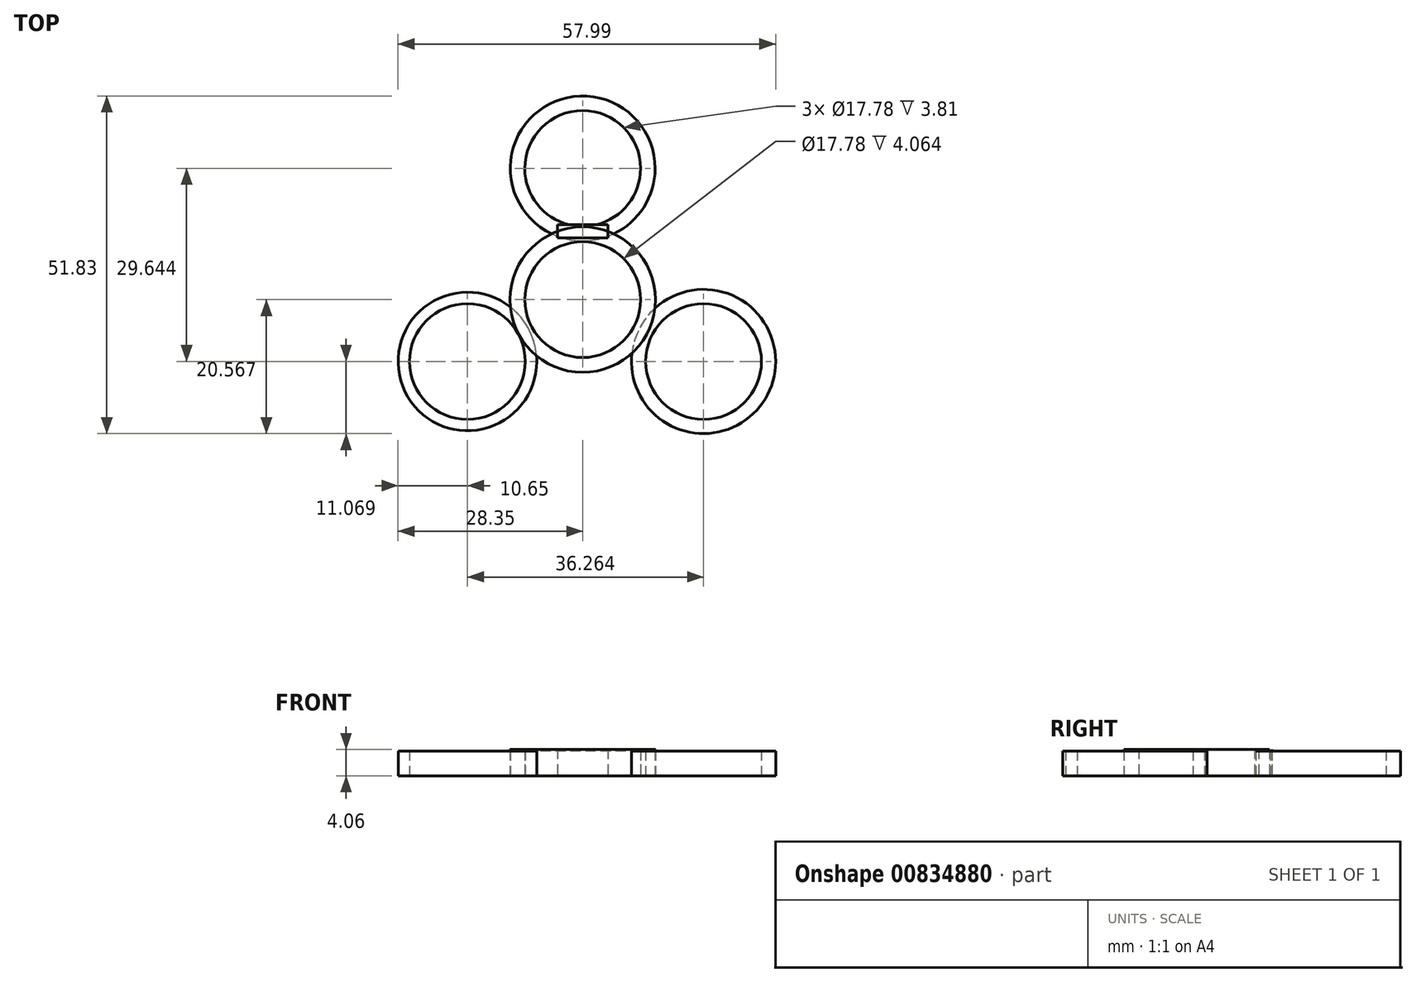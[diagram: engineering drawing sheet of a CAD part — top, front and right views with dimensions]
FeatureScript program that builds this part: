
annotation { "Feature Type Name" : "Feature", "Feature Type Description" : "" }
export const myFeature = defineFeature(function(context is Context, id is Id, definition is map)
    precondition{}
    {
        {
            var Q0;
            Q0=qCreatedBy(makeId("Top.planeOp"),FACE);
            var sketch = newSketch(context, id + "F0", { "sketchPlane" : qUnion([Q0])});
            skCircle(sketch, "E0", {"center": v(0, 25.18) * mm, "radius": 11.12 * mm});
            skCircle(sketch, "E1", {"center": v(-17.7, -4.46) * mm, "radius": 10.65 * mm});
            skCircle(sketch, "E2", {"center": v(18.56, -4.46) * mm, "radius": 11.07 * mm});
            skSolve(sketch);
        }
        {
            var Q0;
            Q0 = qSketchRegion(id + "F0", true);
            extrude(context, id + "F1", {"entities" : qUnion([Q0]), "depth" : 3.8 * mm, "offsetDistance" : 25.4 * mm});
        }
        {
            var Q0;
            Q0=sQuery(id+"F0.wireOp",VERTEX,"E0.center");
            var Q1;
            Q1=sQuery(id+"F0.wireOp",VERTEX,"E1.center");
            var Q2;
            Q2=sQuery(id+"F0.wireOp",VERTEX,"E2.center");
            var Q3;
            Q3=makeQuery(id+"F1.opExtrude","SWEPT_BODY",BODY,{"disambiguationData":[OSD([sQuery(id+"F0.wireOp",EDGE,"E0")])]});
            var Q4;
            Q4=makeQuery(id+"F1.opExtrude","SWEPT_BODY",BODY,{"disambiguationData":[OSD([sQuery(id+"F0.wireOp",EDGE,"E1")])]});
            var Q5;
            Q5=makeQuery(id+"F1.opExtrude","SWEPT_BODY",BODY,{"disambiguationData":[OSD([sQuery(id+"F0.wireOp",EDGE,"E2")])]});
            hole(context, id + "F2", {"style" : HoleStyle.SIMPLE, "endStyle" : HoleEndStyle.THROUGH, "oppositeDirection" : true, "holeDiameter" : 17.78 * mm, "majorDiameter" : 6.35 * mm, "isTappedThrough" : true, "tappedDepth" : 12.7 * mm, "tapClearance" : 3, "locations" : qUnion([Q0, Q1, Q2]), "scope" : qUnion([Q3, Q4, Q5])});
        }
        {
            var Q0;
            Q0=qCreatedBy(makeId("Top.planeOp"),FACE);
            var sketch = newSketch(context, id + "F3", { "sketchPlane" : qUnion([Q0])});
            skCircle(sketch, "E3", {"center": v(0, 5.04) * mm, "radius": 11.17 * mm});
            skSolve(sketch);
        }
        {
            var Q0;
            Q0 = qSketchRegion(id + "F3", true);
            extrude(context, id + "F4", {"entities" : qUnion([Q0]), "depth" : 4.06 * mm, "offsetDistance" : 25.4 * mm});
        }
        {
            var Q0;
            Q0=sQuery(id+"F3.wireOp",VERTEX,"E3.center");
            var Q1;
            Q1=makeQuery(id+"F4.opExtrude","SWEPT_BODY",BODY,{"disambiguationData":[OSD([sQuery(id+"F3.wireOp",EDGE,"E3")])]});
            hole(context, id + "F5", {"style" : HoleStyle.SIMPLE, "endStyle" : HoleEndStyle.THROUGH, "oppositeDirection" : true, "holeDiameter" : 17.78 * mm, "majorDiameter" : 6.35 * mm, "isTappedThrough" : true, "tappedDepth" : 12.7 * mm, "tapClearance" : 3, "locations" : qUnion([Q0]), "scope" : qUnion([Q1])});
        }
        {
            var Q0;
            Q0=qCreatedBy(makeId("Top.planeOp"),FACE);
            var sketch = newSketch(context, id + "F6", { "sketchPlane" : qUnion([Q0])});
            skLineSegment(sketch, "E4.bottom", {"start": v(-3.89, 16.55) * mm, "end": v(3.89, 16.55) * mm});
            skLineSegment(sketch, "E4.top", {"start": v(-3.89, 14.53) * mm, "end": v(3.89, 14.53) * mm});
            skLineSegment(sketch, "E4.left", {"start": v(-3.89, 16.55) * mm, "end": v(-3.89, 14.53) * mm});
            skLineSegment(sketch, "E4.right", {"start": v(3.89, 16.55) * mm, "end": v(3.89, 14.53) * mm});
            skSolve(sketch);
        }
        {
            var Q0;
            Q0 = qSketchRegion(id + "F6", true);
            extrude(context, id + "F7", {"entities" : qUnion([Q0]), "depth" : 4.06 * mm, "offsetDistance" : 25.4 * mm});
        }
    });
